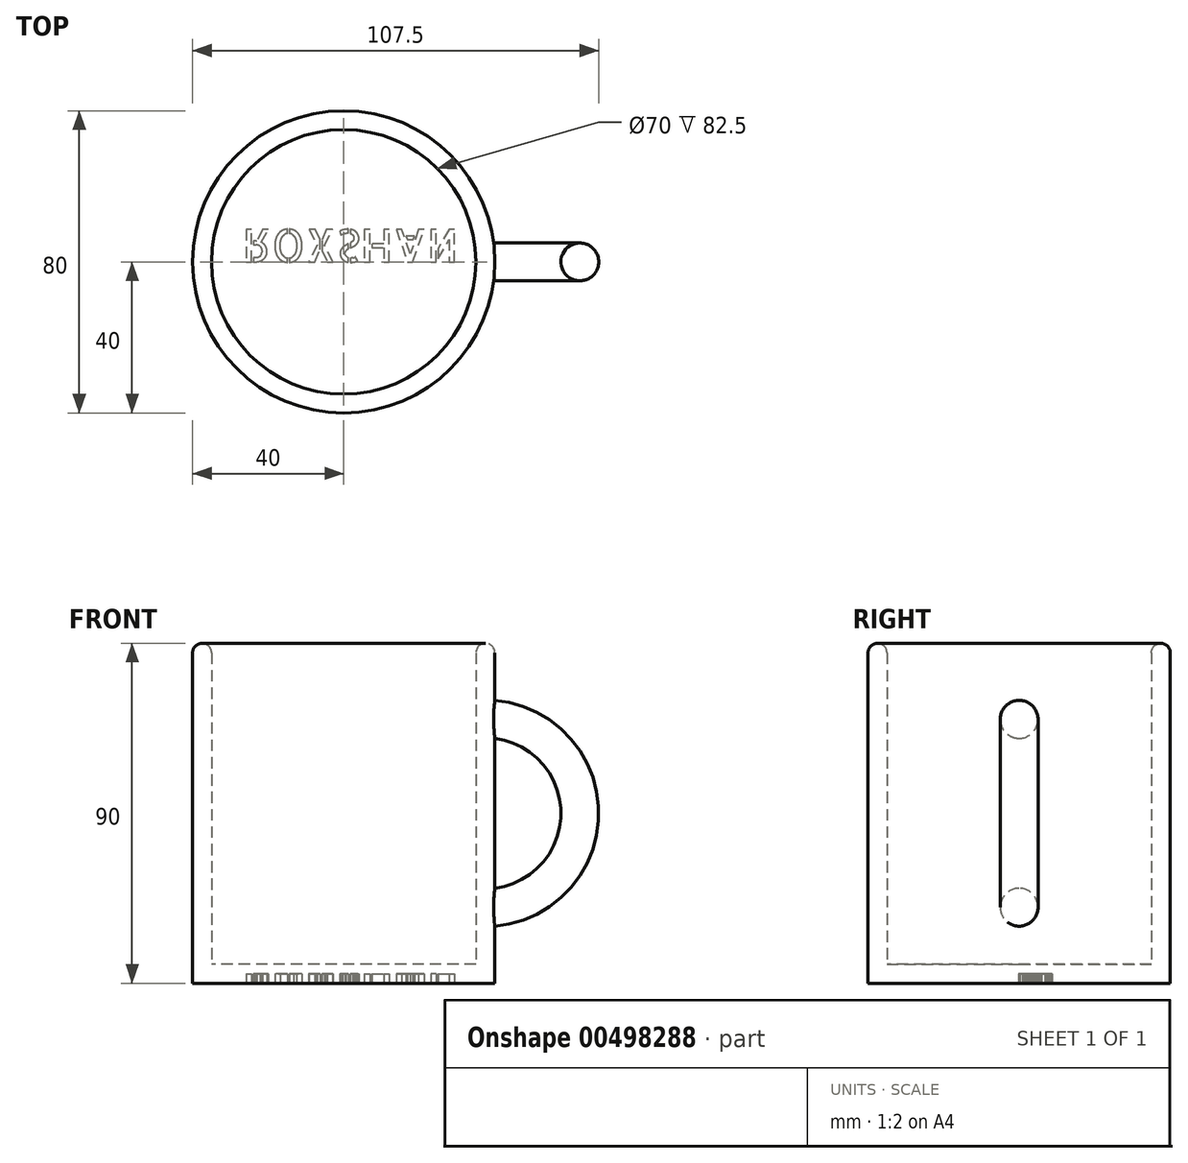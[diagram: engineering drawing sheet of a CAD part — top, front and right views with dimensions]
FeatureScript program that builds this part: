
annotation { "Feature Type Name" : "Feature", "Feature Type Description" : "" }
export const myFeature = defineFeature(function(context is Context, id is Id, definition is map)
    precondition{}
    {
        {
            var Q0;
            Q0=qCreatedBy(makeId("Top.planeOp"),FACE);
            var sketch = newSketch(context, id + "F0", { "sketchPlane" : qUnion([Q0])});
            skCircle(sketch, "E0", {"center": v(0, 0) * mm, "radius": 40 * mm});
            skSolve(sketch);
        }
        {
            var Q0;
            Q0 = qSketchRegion(id + "F0", true);
            extrude(context, id + "F1", {"entities" : qUnion([Q0]), "depth" : 90 * mm});
        }
        {
            var Q0;
            Q0=makeQuery(id+"F1.opExtrude","CAP_FACE",FACE,{"disambiguationData":[OSD([sQuery(id+"F0.wireOp",EDGE,"E0")])],"isStart":false});
            shell(context, id + "F2", {"entities" : qUnion([Q0]), "thickness" : 5 * mm});
        }
        {
            var Q0;
            Q0=qCreatedBy(makeId("Right.planeOp"),FACE);
            cPlane(context, id + "F3", {"entities" : qUnion([Q0]), "cplaneType" : CPlaneType.OFFSET, "offset" : 37.5 * mm, "width" : 150 * mm, "height" : 150 * mm});
        }
        {
            var Q0;
            Q0=qCreatedBy(id+"F3.planeOp",FACE);
            var sketch = newSketch(context, id + "F4", { "sketchPlane" : qUnion([Q0])});
            skCircle(sketch, "E1", {"center": v(0, 70) * mm, "radius": 5 * mm});
            skLineSegment(sketch, "E2", {"start": v(0, 45) * mm, "end": v(36, 45) * mm});
            skSolve(sketch);
        }
        {
            var Q0;
            Q0 = qSketchRegion(id + "F4", true);
            var Q1;
            Q1=sQuery(id+"F4.wireOp",EDGE,"E2");
            revolve(context, id + "F5", {"operationType" : NewBodyOperationType.ADD, "entities" : qUnion([Q0]), "axis" : qUnion([Q1]), "revolveType" : RevolveType.ONE_DIRECTION, "angle" : 180 * degree});
        }
        {
            var Q0;
            {var subQ0=sQuery(id+"F0.wireOp",EDGE,"E0");Q0=makeQuery(id+"F2.opShell","OFFSET_EDGE",EDGE,{"disambiguationData":[OSD([subQ0]),TDD([makeQuery(id+"F1.opExtrude","CAP_EDGE",EDGE,{"disambiguationData":[OSD([subQ0])],"isStart":false})])]});}
            var Q1;
            Q1=makeQuery(id+"F1.opExtrude","CAP_EDGE",EDGE,{"disambiguationData":[OSD([sQuery(id+"F0.wireOp",EDGE,"E0")])],"isStart":false});
            fillet(context, id + "F6", {"entities" : qUnion([Q0, Q1]), "radius" : 2.5 * mm, "tangentPropagation" : true, "allowEdgeOverflow" : false});
        }
        {
            var Q0;
            Q0=makeQuery(id+"F1.opExtrude","CAP_FACE",FACE,{"disambiguationData":[OSD([sQuery(id+"F0.wireOp",EDGE,"E0")])],"isStart":true});
            var sketch = newSketch(context, id + "F7", { "sketchPlane" : qUnion([Q0])});
            skText(sketch, "E3", { "text": "ROXSHAN", "fontName": "OpenSans-BoldItalic.ttf"});
            const initialGuessF7  = {"E3": [-0.02451, -0.00713, 1, 0, 0.00713]};
            skSetInitialGuess(sketch, initialGuessF7);
            skSolve(sketch);
        }
        {
            var Q0;
            Q0 = qSketchRegion(id + "F7", true);
            extrude(context, id + "F8", {"entities" : qUnion([Q0]), "operationType" : NewBodyOperationType.ADD, "oppositeDirection" : true, "depth" : 2.5 * mm});
        }
        {
            var Q0;
            Q0=makeQuery(id+"F1.opExtrude","CAP_FACE",FACE,{"disambiguationData":[OSD([sQuery(id+"F0.wireOp",EDGE,"E0")])],"isStart":true});
            var sketch = newSketch(context, id + "F9", { "sketchPlane" : qUnion([Q0])});
            skText(sketch, "E4", { "text": "ROXSHAN", "fontName": "AllertaStencil-Regular.ttf"});
            const initialGuessF9  = {"E4": [-0.02685, -0.00862, 1, 0, 0.00862]};
            skSetInitialGuess(sketch, initialGuessF9);
            skSolve(sketch);
        }
        {
            var Q0;
            Q0 = qSketchRegion(id + "F9", true);
            extrude(context, id + "F10", {"entities" : qUnion([Q0]), "operationType" : NewBodyOperationType.REMOVE, "oppositeDirection" : true, "depth" : 2.5 * mm});
        }
    });
